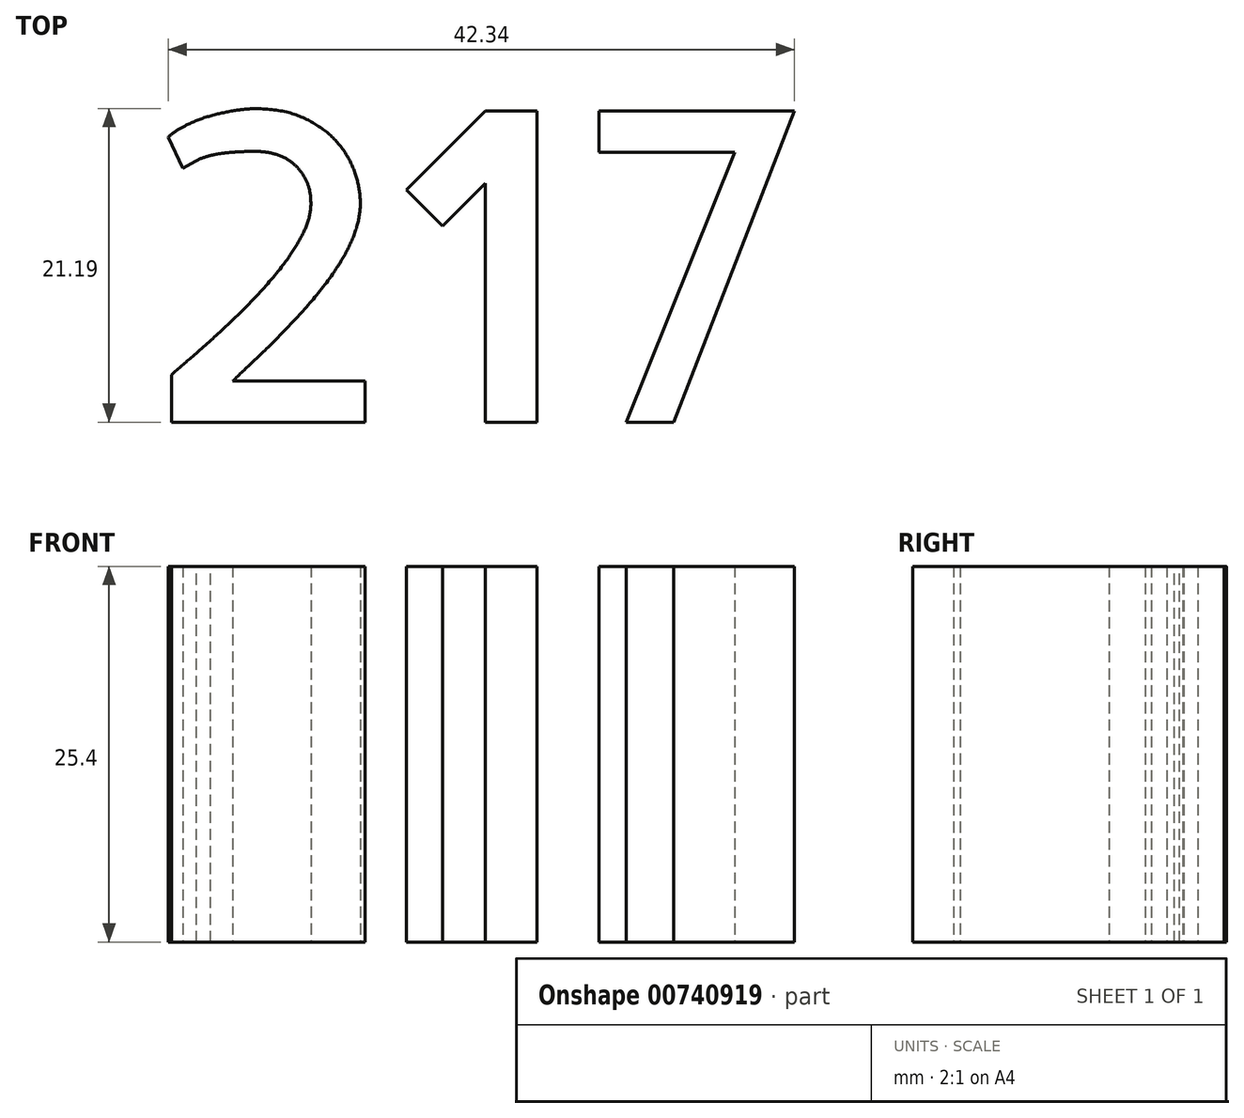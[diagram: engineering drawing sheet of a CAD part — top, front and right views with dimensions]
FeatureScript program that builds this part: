
annotation { "Feature Type Name" : "Feature", "Feature Type Description" : "" }
export const myFeature = defineFeature(function(context is Context, id is Id, definition is map)
    precondition{}
    {
        {
            var Q0;
            Q0=qCreatedBy(makeId("Top.planeOp"),FACE);
            var sketch = newSketch(context, id + "F0", { "sketchPlane" : qUnion([Q0])});
            skText(sketch, "E0", { "text": "217", "fontName": "AllertaStencil-Regular.ttf"});
            const initialGuessF0  = {"E0": [-0.02628, -0.01034, 1, 0, 0.02105]};
            skSetInitialGuess(sketch, initialGuessF0);
            skSolve(sketch);
        }
        {
            var Q0;
            Q0 = qSketchRegion(id + "F0", true);
            extrude(context, id + "F1", {"entities" : qUnion([Q0]), "depth" : 25.4 * mm, "offsetDistance" : 25.4 * mm});
        }
    });
